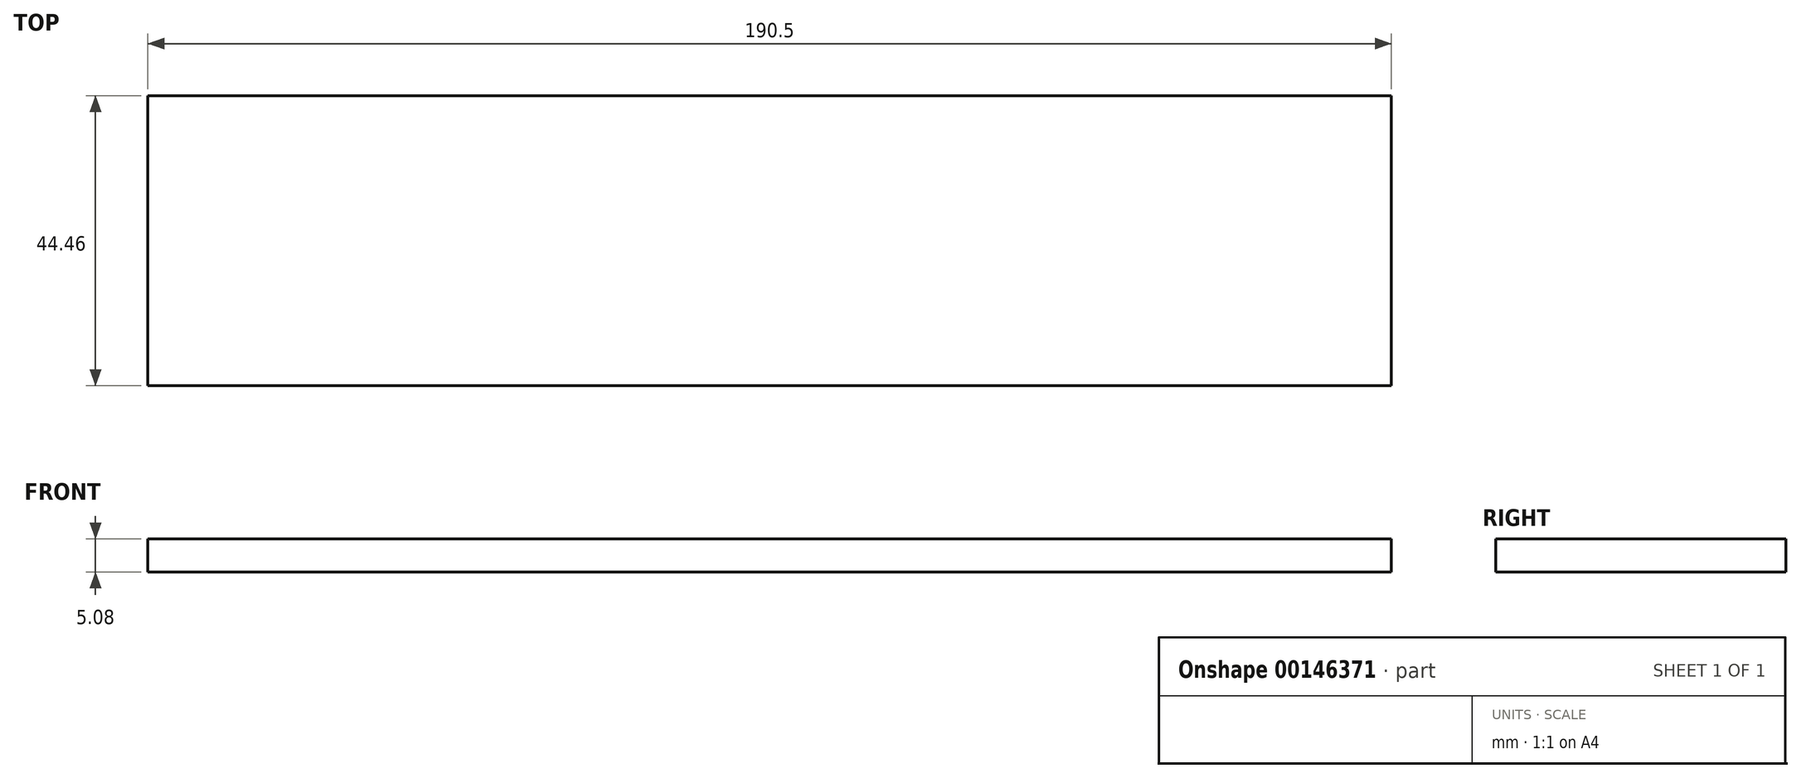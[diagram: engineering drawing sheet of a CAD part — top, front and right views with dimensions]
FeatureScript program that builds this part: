
annotation { "Feature Type Name" : "Feature", "Feature Type Description" : "" }
export const myFeature = defineFeature(function(context is Context, id is Id, definition is map)
    precondition{}
    {
        {
            var Q0;
            Q0=qCreatedBy(makeId("Top.planeOp"),FACE);
            var sketch = newSketch(context, id + "F0", { "sketchPlane" : qUnion([Q0])});
            skLineSegment(sketch, "E0.bottom", {"start": v(95.25, 22.23) * mm, "end": v(-95.25, 22.23) * mm});
            skLineSegment(sketch, "E0.top", {"start": v(95.25, -22.23) * mm, "end": v(-95.25, -22.23) * mm});
            skLineSegment(sketch, "E0.left", {"start": v(95.25, 22.23) * mm, "end": v(95.25, -22.23) * mm});
            skLineSegment(sketch, "E0.right", {"start": v(-95.25, 22.23) * mm, "end": v(-95.25, -22.23) * mm});
            skPoint(sketch, "E0.middle", {"position": v(0, 0) * mm});
            skSolve(sketch);
        }
        {
            var Q0;
            Q0=makeQuery(id+"F0.imprint","IMPRINT",FACE,{"disambiguationData":[TD([[makeQuery(id+"F0.imprint","IMPRINT",EDGE,{"derivedFrom":sQuery(id+"F0.wireOp",EDGE,"E0.bottom")}),1.0]])]});
            extrude(context, id + "F1", {"entities" : qUnion([Q0]), "depth" : 5.08 * mm});
        }
    });
